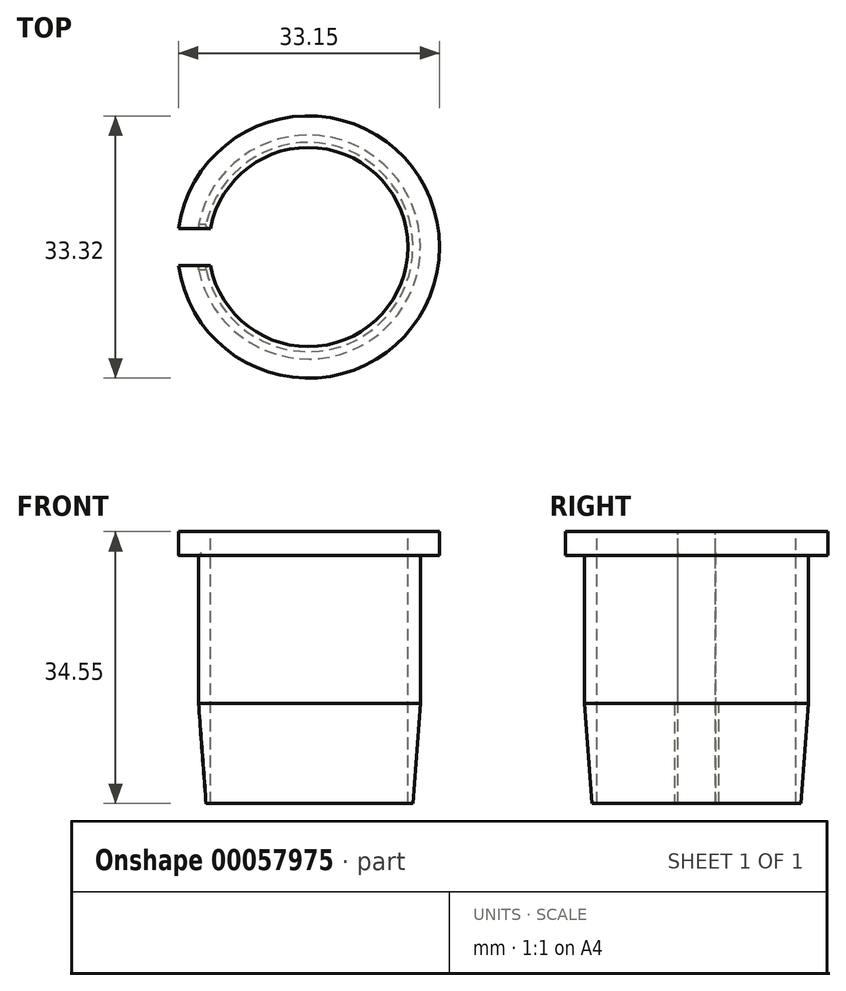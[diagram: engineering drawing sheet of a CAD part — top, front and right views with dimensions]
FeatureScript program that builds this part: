
annotation { "Feature Type Name" : "Feature", "Feature Type Description" : "" }
export const myFeature = defineFeature(function(context is Context, id is Id, definition is map)
    precondition{}
    {
        {
            var Q0;
            Q0=qCreatedBy(makeId("Right.planeOp"),FACE);
            var sketch = newSketch(context, id + "F0", { "sketchPlane" : qUnion([Q0])});
            skLineSegment(sketch, "E0", {"start": v(0, 34.7) * mm, "end": v(0, -25.4) * mm, "construction": true});
            skLineSegment(sketch, "E1", {"start": v(-12.65, 34.7) * mm, "end": v(-16.66, 34.7) * mm});
            skLineSegment(sketch, "E2", {"start": v(-16.66, 34.7) * mm, "end": v(-16.66, 31.5) * mm});
            skLineSegment(sketch, "E3", {"start": v(-16.66, 31.65) * mm, "end": v(-14.22, 31.65) * mm});
            skLineSegment(sketch, "E4", {"start": v(-14.22, 31.65) * mm, "end": v(-14.22, 12.85) * mm});
            skLineSegment(sketch, "E5", {"start": v(-16.66, -24.6) * mm, "end": v(-16.66, -24.61) * mm});
            skLineSegment(sketch, "E6", {"start": v(-12.65, 34.7) * mm, "end": v(-12.65, 0.15) * mm});
            skPoint(sketch, "E7.visualSharp", {"position": v(-12.65, 34.7) * mm});
            skPoint(sketch, "E8.visualSharp", {"position": v(-16.66, 34.7) * mm});
            skPoint(sketch, "E9.visualSharp", {"position": v(-16.66, 31.65) * mm});
            skLineSegment(sketch, "E10", {"start": v(-12.65, 0.15) * mm, "end": v(-13.28, 0.15) * mm});
            skLineSegment(sketch, "E11", {"start": v(-14.22, 12.85) * mm, "end": v(-13.28, 0.15) * mm});
            skSolve(sketch);
        }
        {
            var Q0;
            Q0 = qSketchRegion(id + "F0", true);
            var Q1;
            Q1=sQuery(id+"F0.wireOp",EDGE,"E0");
            revolve(context, id + "F1", {"entities" : qUnion([Q0]), "axis" : qUnion([Q1]), "revolveType" : RevolveType.FULL});
        }
        {
            var Q0;
            Q0=qCreatedBy(makeId("Top.planeOp"),FACE);
            var sketch = newSketch(context, id + "F2", { "sketchPlane" : qUnion([Q0])});
            skLineSegment(sketch, "E12.rect.bottom", {"start": v(-25.4, 2.37) * mm, "end": v(-0.25, 2.37) * mm});
            skLineSegment(sketch, "E12.rect.top", {"start": v(-25.4, -2.37) * mm, "end": v(-0.25, -2.37) * mm});
            skLineSegment(sketch, "E12.rect.left", {"start": v(-25.4, 2.37) * mm, "end": v(-25.4, -2.37) * mm});
            skPoint(sketch, "E12.rect.middle", {"position": v(0, 0) * mm});
            skLineSegment(sketch, "E13", {"start": v(-0.25, -2.37) * mm, "end": v(-0.25, 2.37) * mm});
            skSolve(sketch);
        }
        {
            var Q0;
            Q0=qSketchRegion(id+"F2",true);
            extrude(context, id + "F3", {"entities" : qUnion([Q0]), "operationType" : NewBodyOperationType.REMOVE, "endBound" : BoundingType.THROUGH_ALL, "depth" : 50.8 * mm});
        }
        {
            var Q0;
            Q0=makeQuery(id+"F3.boolean.opBoolean","INTERSECT",EDGE,{"derivedFrom":[makeQuery(id+"F1.opRevolve","SWEPT_FACE",FACE,{"disambiguationData":[OSD([sQuery(id+"F0.wireOp",EDGE,"E11")])]}),makeQuery(id+"F3.opExtrude","SWEPT_FACE",FACE,{"disambiguationData":[OSD([sQuery(id+"F2.wireOp",EDGE,"E12.rect.top")])]})]});
            var Q1;
            Q1=makeQuery(id+"F3.boolean.opBoolean","INTERSECT",EDGE,{"derivedFrom":[makeQuery(id+"F1.opRevolve","SWEPT_FACE",FACE,{"disambiguationData":[OSD([sQuery(id+"F0.wireOp",EDGE,"E4")])]}),makeQuery(id+"F3.opExtrude","SWEPT_FACE",FACE,{"disambiguationData":[OSD([sQuery(id+"F2.wireOp",EDGE,"E12.rect.top")])]})]});
            var Q2;
            Q2=makeQuery(id+"F3.boolean.opBoolean","INTERSECT",EDGE,{"derivedFrom":[makeQuery(id+"F1.opRevolve","SWEPT_FACE",FACE,{"disambiguationData":[OSD([sQuery(id+"F0.wireOp",EDGE,"E11")])]}),makeQuery(id+"F3.opExtrude","SWEPT_FACE",FACE,{"disambiguationData":[OSD([sQuery(id+"F2.wireOp",EDGE,"E12.rect.bottom")])]})]});
            var Q3;
            Q3=makeQuery(id+"F3.boolean.opBoolean","INTERSECT",EDGE,{"derivedFrom":[makeQuery(id+"F1.opRevolve","SWEPT_FACE",FACE,{"disambiguationData":[OSD([sQuery(id+"F0.wireOp",EDGE,"E4")])]}),makeQuery(id+"F3.opExtrude","SWEPT_FACE",FACE,{"disambiguationData":[OSD([sQuery(id+"F2.wireOp",EDGE,"E12.rect.bottom")])]})]});
            var Q4;
            Q4=makeQuery(id+"F3.boolean.opBoolean","INTERSECT",EDGE,{"derivedFrom":[makeQuery(id+"F1.opRevolve","SWEPT_FACE",FACE,{"disambiguationData":[OSD([sQuery(id+"F0.wireOp",EDGE,"E3")])]}),makeQuery(id+"F3.opExtrude","SWEPT_FACE",FACE,{"disambiguationData":[OSD([sQuery(id+"F2.wireOp",EDGE,"E12.rect.top")])]})]});
            var Q5;
            Q5=makeQuery(id+"F3.boolean.opBoolean","INTERSECT",EDGE,{"derivedFrom":[makeQuery(id+"F1.opRevolve","SWEPT_FACE",FACE,{"disambiguationData":[OSD([sQuery(id+"F0.wireOp",EDGE,"E3")])]}),makeQuery(id+"F3.opExtrude","SWEPT_FACE",FACE,{"disambiguationData":[OSD([sQuery(id+"F2.wireOp",EDGE,"E12.rect.bottom")])]})]});
            fillet(context, id + "F4", {"entities" : qUnion([Q0, Q1, Q2, Q3, Q4, Q5]), "radius" : 0.38 * mm, "tangentPropagation" : true, "allowEdgeOverflow" : false});
        }
    });
